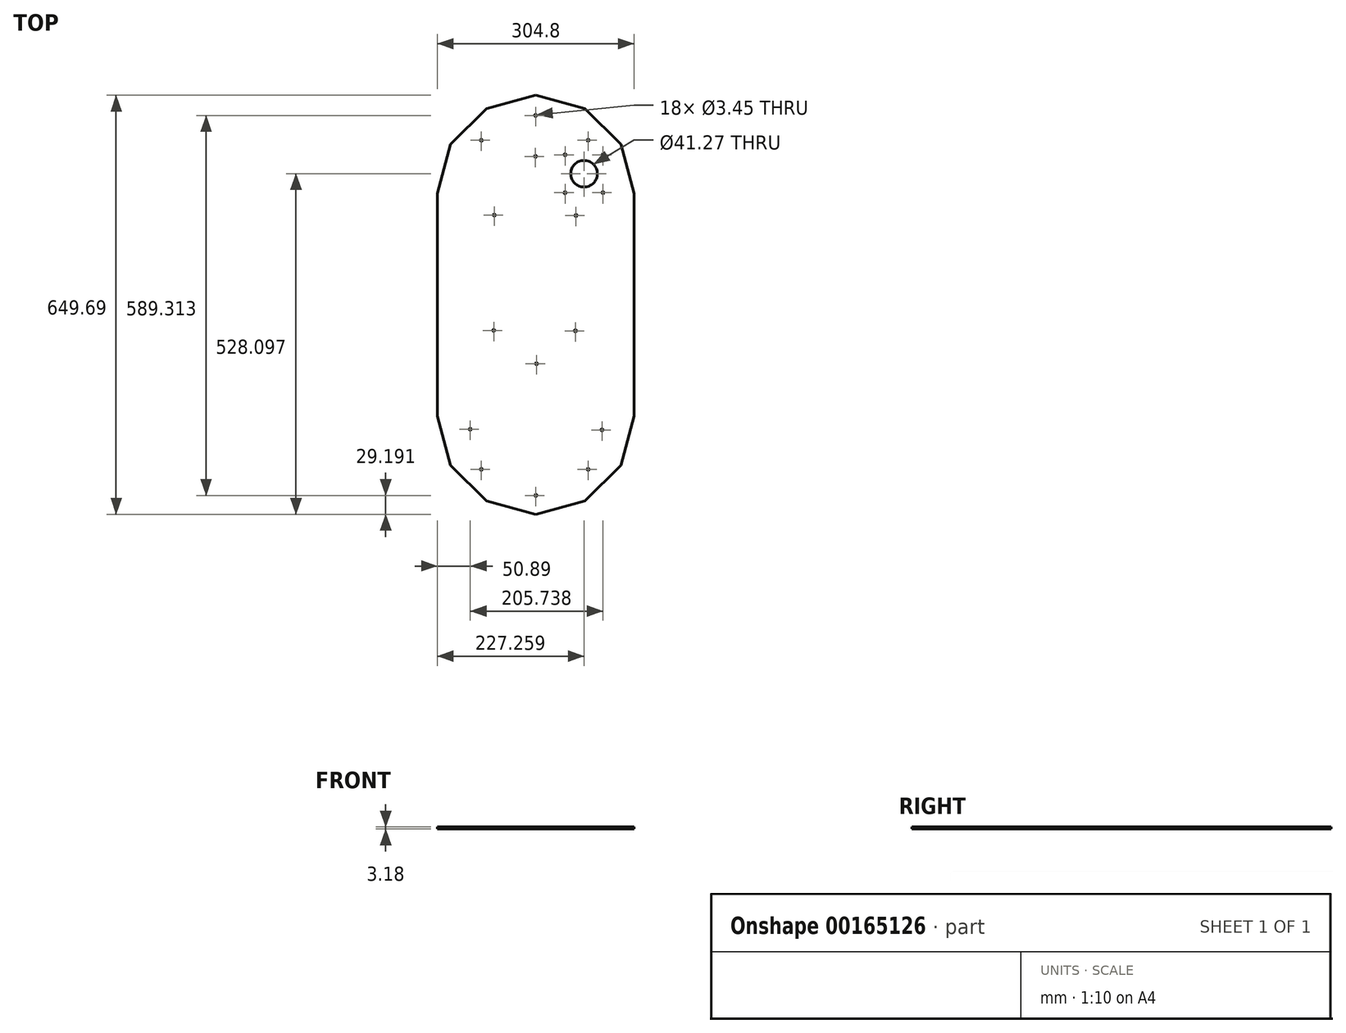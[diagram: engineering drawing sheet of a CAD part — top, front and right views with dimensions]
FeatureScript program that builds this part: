
annotation { "Feature Type Name" : "Feature", "Feature Type Description" : "" }
export const myFeature = defineFeature(function(context is Context, id is Id, definition is map)
    precondition{}
    {
        {
            var Q0;
            Q0=qCreatedBy(makeId("Top.planeOp"),FACE);
            var sketch = newSketch(context, id + "F0", { "sketchPlane" : qUnion([Q0])});
            skLineSegment(sketch, "E0", {"start": v(152.4, 0) * mm, "end": v(304.8, 0) * mm, "construction": true});
            skLineSegment(sketch, "E1", {"start": v(152.4, 0) * mm, "end": v(284.38, 76.2) * mm, "construction": true});
            skLineSegment(sketch, "E2", {"start": v(152.4, 0) * mm, "end": v(228.6, 131.98) * mm, "construction": true});
            skLineSegment(sketch, "E3", {"start": v(152.4, 0) * mm, "end": v(152.4, 152.4) * mm, "construction": true});
            skLineSegment(sketch, "E4", {"start": v(304.8, 0) * mm, "end": v(284.38, 76.2) * mm});
            skLineSegment(sketch, "E5", {"start": v(284.38, 76.2) * mm, "end": v(228.6, 131.98) * mm});
            skLineSegment(sketch, "E6", {"start": v(228.6, 131.98) * mm, "end": v(152.4, 152.4) * mm});
            skLineSegment(sketch, "E7", {"start": v(304.8, 0) * mm, "end": v(304.8, -344.89) * mm});
            skLineSegment(sketch, "E8", {"start": v(304.8, -344.89) * mm, "end": v(152.4, -344.89) * mm, "construction": true});
            skLineSegment(sketch, "E9", {"start": v(152.4, -344.89) * mm, "end": v(284.38, -421.09) * mm, "construction": true});
            skLineSegment(sketch, "E10", {"start": v(152.4, 0) * mm, "end": v(76.2, 131.98) * mm, "construction": true});
            skLineSegment(sketch, "E11", {"start": v(152.4, 0) * mm, "end": v(20.42, 76.2) * mm, "construction": true});
            skLineSegment(sketch, "E12", {"start": v(152.4, 0) * mm, "end": v(0, 0) * mm, "construction": true});
            skLineSegment(sketch, "E13", {"start": v(152.4, -344.89) * mm, "end": v(0, -344.89) * mm, "construction": true});
            skLineSegment(sketch, "E14", {"start": v(152.4, 152.4) * mm, "end": v(76.2, 131.98) * mm});
            skLineSegment(sketch, "E15", {"start": v(76.2, 131.98) * mm, "end": v(20.42, 76.2) * mm});
            skLineSegment(sketch, "E16", {"start": v(20.42, 76.2) * mm, "end": v(0, 0) * mm});
            skLineSegment(sketch, "E17", {"start": v(0, 0) * mm, "end": v(0, -344.89) * mm});
            skLineSegment(sketch, "E18", {"start": v(152.4, -344.89) * mm, "end": v(228.6, -476.87) * mm, "construction": true});
            skLineSegment(sketch, "E19", {"start": v(152.4, -344.89) * mm, "end": v(152.4, -497.29) * mm, "construction": true});
            skLineSegment(sketch, "E20", {"start": v(152.4, -344.89) * mm, "end": v(76.2, -476.87) * mm, "construction": true});
            skLineSegment(sketch, "E21", {"start": v(152.4, -344.89) * mm, "end": v(20.42, -421.09) * mm, "construction": true});
            skLineSegment(sketch, "E22", {"start": v(0, -344.89) * mm, "end": v(20.42, -421.09) * mm});
            skLineSegment(sketch, "E23", {"start": v(20.42, -421.09) * mm, "end": v(76.2, -476.87) * mm});
            skLineSegment(sketch, "E24", {"start": v(76.2, -476.87) * mm, "end": v(152.4, -497.29) * mm});
            skLineSegment(sketch, "E25", {"start": v(152.4, -497.29) * mm, "end": v(228.6, -476.87) * mm});
            skLineSegment(sketch, "E26", {"start": v(228.6, -476.87) * mm, "end": v(284.38, -421.09) * mm});
            skLineSegment(sketch, "E27", {"start": v(284.38, -421.09) * mm, "end": v(304.8, -344.89) * mm});
            skSolve(sketch);
        }
        {
            var Q0;
            Q0=qSketchRegion(id+"F0",true);
            extrude(context, id + "F1", {"entities" : qUnion([Q0]), "depth" : 3.17 * mm});
        }
        {
            var Q0;
            Q0=makeQuery(id+"F1.opExtrude","CAP_FACE",FACE,{"disambiguationData":[OSD([sQuery(id+"F0.wireOp",EDGE,"E4"),sQuery(id+"F0.wireOp",EDGE,"E5"),sQuery(id+"F0.wireOp",EDGE,"E6"),sQuery(id+"F0.wireOp",EDGE,"E7"),sQuery(id+"F0.wireOp",EDGE,"E14"),sQuery(id+"F0.wireOp",EDGE,"E15"),sQuery(id+"F0.wireOp",EDGE,"E16"),sQuery(id+"F0.wireOp",EDGE,"E17"),sQuery(id+"F0.wireOp",EDGE,"E22"),sQuery(id+"F0.wireOp",EDGE,"E23"),sQuery(id+"F0.wireOp",EDGE,"E24"),sQuery(id+"F0.wireOp",EDGE,"E25"),sQuery(id+"F0.wireOp",EDGE,"E26"),sQuery(id+"F0.wireOp",EDGE,"E27")])],"isStart":false});
            var sketch = newSketch(context, id + "F2", { "sketchPlane" : qUnion([Q0])});
            skLineSegment(sketch, "E28.bottom", {"start": v(256.63, 60.18) * mm, "end": v(197.9, 60.18) * mm, "construction": true});
            skLineSegment(sketch, "E28.top", {"start": v(256.63, 1.44) * mm, "end": v(197.9, 1.44) * mm, "construction": true});
            skLineSegment(sketch, "E28.left", {"start": v(256.63, 60.18) * mm, "end": v(256.63, 1.44) * mm, "construction": true});
            skLineSegment(sketch, "E28.right", {"start": v(197.9, 60.18) * mm, "end": v(197.9, 1.44) * mm, "construction": true});
            skPoint(sketch, "E28.middle", {"position": v(227.26, 30.8) * mm});
            skCircle(sketch, "E29", {"center": v(227.26, 30.8) * mm, "radius": 20.64 * mm});
            skLineSegment(sketch, "E30", {"start": v(151.06, -123.06) * mm, "end": v(88.2, -33.36) * mm, "construction": true});
            skLineSegment(sketch, "E31", {"start": v(151.5, -33.67) * mm, "end": v(214.8, -33.98) * mm, "construction": true});
            skLineSegment(sketch, "E32", {"start": v(214.8, -33.98) * mm, "end": v(151.06, -123.06) * mm, "construction": true});
            skLineSegment(sketch, "E33", {"start": v(151.06, -123.06) * mm, "end": v(87.32, -212.15) * mm, "construction": true});
            skLineSegment(sketch, "E34", {"start": v(213.93, -212.76) * mm, "end": v(151.06, -123.06) * mm, "construction": true});
            skCircle(sketch, "E35", {"center": v(88.2, -33.36) * mm, "radius": 1.73 * mm});
            skCircle(sketch, "E36", {"center": v(214.8, -33.98) * mm, "radius": 1.73 * mm});
            skCircle(sketch, "E37", {"center": v(197.9, 1.44) * mm, "radius": 1.73 * mm});
            skCircle(sketch, "E38", {"center": v(256.63, 1.44) * mm, "radius": 1.73 * mm});
            skCircle(sketch, "E39", {"center": v(256.63, 60.18) * mm, "radius": 1.73 * mm});
            skCircle(sketch, "E40", {"center": v(197.9, 60.18) * mm, "radius": 1.73 * mm});
            skCircle(sketch, "E41", {"center": v(213.93, -212.76) * mm, "radius": 1.73 * mm});
            skCircle(sketch, "E42", {"center": v(87.32, -212.15) * mm, "radius": 1.73 * mm});
            skLineSegment(sketch, "E43", {"start": v(151.06, -123.06) * mm, "end": v(151.5, -33.67) * mm, "construction": true});
            skLineSegment(sketch, "E44", {"start": v(151.06, -123.06) * mm, "end": v(150.62, -212.46) * mm, "construction": true});
            skLineSegment(sketch, "E45", {"start": v(150.62, -212.46) * mm, "end": v(213.93, -212.76) * mm, "construction": true});
            skLineSegment(sketch, "E46", {"start": v(150.62, -212.46) * mm, "end": v(87.32, -212.15) * mm, "construction": true});
            skLineSegment(sketch, "E47", {"start": v(151.5, -33.67) * mm, "end": v(88.2, -33.36) * mm, "construction": true});
            skLineSegment(sketch, "E48.bottom", {"start": v(50.9, -365.45) * mm, "end": v(153.54, -263.8) * mm, "construction": true});
            skLineSegment(sketch, "E48.top", {"start": v(152.54, -468.1) * mm, "end": v(255.19, -366.45) * mm, "construction": true});
            skLineSegment(sketch, "E48.left", {"start": v(50.9, -365.45) * mm, "end": v(152.54, -468.1) * mm, "construction": true});
            skLineSegment(sketch, "E48.right", {"start": v(153.54, -263.8) * mm, "end": v(255.19, -366.45) * mm, "construction": true});
            skPoint(sketch, "E48.middle", {"position": v(153.04, -365.95) * mm});
            skLineSegment(sketch, "E49", {"start": v(152.4, -497.29) * mm, "end": v(152.54, -468.1) * mm, "construction": true});
            skLineSegment(sketch, "E50", {"start": v(152.54, -468.1) * mm, "end": v(153.54, -263.8) * mm, "construction": true});
            skCircle(sketch, "E51", {"center": v(152.54, -468.1) * mm, "radius": 1.73 * mm});
            skCircle(sketch, "E52", {"center": v(255.19, -366.45) * mm, "radius": 1.73 * mm});
            skCircle(sketch, "E53", {"center": v(153.54, -263.8) * mm, "radius": 1.73 * mm});
            skCircle(sketch, "E54", {"center": v(50.9, -365.45) * mm, "radius": 1.73 * mm});
            skLineSegment(sketch, "E55", {"start": v(294.6, 38.1) * mm, "end": v(270.06, 31.53) * mm, "construction": true});
            skLineSegment(sketch, "E56", {"start": v(256.5, 104.1) * mm, "end": v(238.53, 86.13) * mm, "construction": true});
            skLineSegment(sketch, "E57", {"start": v(238.53, 86.13) * mm, "end": v(261.6, 63.05) * mm, "construction": true});
            skLineSegment(sketch, "E58", {"start": v(270.06, 31.53) * mm, "end": v(261.6, 63.05) * mm, "construction": true});
            skCircle(sketch, "E59", {"center": v(256.63, 60.18) * mm, "radius": 5.56 * mm, "construction": true});
            skLineSegment(sketch, "E60", {"start": v(151.5, -33.67) * mm, "end": v(152.4, 152.4) * mm, "construction": true});
            skLineSegment(sketch, "E61", {"start": v(151.06, -123.06) * mm, "end": v(227.26, -123.06) * mm, "construction": true});
            skLineSegment(sketch, "E62", {"start": v(227.26, -123.06) * mm, "end": v(227.26, 30.8) * mm, "construction": true});
            skLineSegment(sketch, "E63", {"start": v(190.5, 142.2) * mm, "end": v(183.93, 117.66) * mm, "construction": true});
            skLineSegment(sketch, "E64", {"start": v(183.93, 117.66) * mm, "end": v(152.27, 126.14) * mm, "construction": true});
            skLineSegment(sketch, "E65", {"start": v(152.27, 126.14) * mm, "end": v(120.87, 117.66) * mm, "construction": true});
            skLineSegment(sketch, "E66", {"start": v(114.3, 142.2) * mm, "end": v(120.87, 117.66) * mm, "construction": true});
            skCircle(sketch, "E67", {"center": v(152.25, 121.21) * mm, "radius": 4.76 * mm, "construction": true});
            skCircle(sketch, "E68", {"center": v(152.25, 121.21) * mm, "radius": 1.73 * mm});
            skCircle(sketch, "E69", {"center": v(151.94, 57.71) * mm, "radius": 1.73 * mm});
            skLineSegment(sketch, "E70.bottom", {"start": v(233.58, 82.76) * mm, "end": v(68.06, 82.76) * mm, "construction": true});
            skLineSegment(sketch, "E70.top", {"start": v(233.58, -427.65) * mm, "end": v(68.06, -427.65) * mm, "construction": true});
            skLineSegment(sketch, "E70.left", {"start": v(233.58, 82.76) * mm, "end": v(233.58, -427.65) * mm, "construction": true});
            skLineSegment(sketch, "E70.right", {"start": v(68.06, 82.76) * mm, "end": v(68.06, -427.65) * mm, "construction": true});
            skPoint(sketch, "E70.middle", {"position": v(150.82, -172.44) * mm});
            skLineSegment(sketch, "E71", {"start": v(0, -172.44) * mm, "end": v(304.8, -172.44) * mm, "construction": true});
            skCircle(sketch, "E72", {"center": v(68.06, 82.76) * mm, "radius": 1.73 * mm});
            skCircle(sketch, "E73", {"center": v(233.58, 82.76) * mm, "radius": 1.73 * mm});
            skCircle(sketch, "E74", {"center": v(68.06, -427.65) * mm, "radius": 1.73 * mm});
            skCircle(sketch, "E75", {"center": v(233.58, -427.65) * mm, "radius": 1.73 * mm});
            skSolve(sketch);
        }
        {
            var Q0;
            Q0=qSketchRegion(id+"F2",true);
            var Q1;
            Q1=makeQuery(id+"F1.opExtrude","CAP_FACE",FACE,{"disambiguationData":[OSD([sQuery(id+"F0.wireOp",EDGE,"E4"),sQuery(id+"F0.wireOp",EDGE,"E5"),sQuery(id+"F0.wireOp",EDGE,"E6"),sQuery(id+"F0.wireOp",EDGE,"E7"),sQuery(id+"F0.wireOp",EDGE,"E14"),sQuery(id+"F0.wireOp",EDGE,"E15"),sQuery(id+"F0.wireOp",EDGE,"E16"),sQuery(id+"F0.wireOp",EDGE,"E17"),sQuery(id+"F0.wireOp",EDGE,"E22"),sQuery(id+"F0.wireOp",EDGE,"E23"),sQuery(id+"F0.wireOp",EDGE,"E24"),sQuery(id+"F0.wireOp",EDGE,"E25"),sQuery(id+"F0.wireOp",EDGE,"E26"),sQuery(id+"F0.wireOp",EDGE,"E27")])],"isStart":true});
            extrude(context, id + "F3", {"entities" : qUnion([Q0]), "operationType" : NewBodyOperationType.REMOVE, "endBound" : BoundingType.UP_TO_SURFACE, "oppositeDirection" : true, "endBoundEntityFace" : qUnion([Q1]), "depth" : 25.4 * mm});
        }
    });
